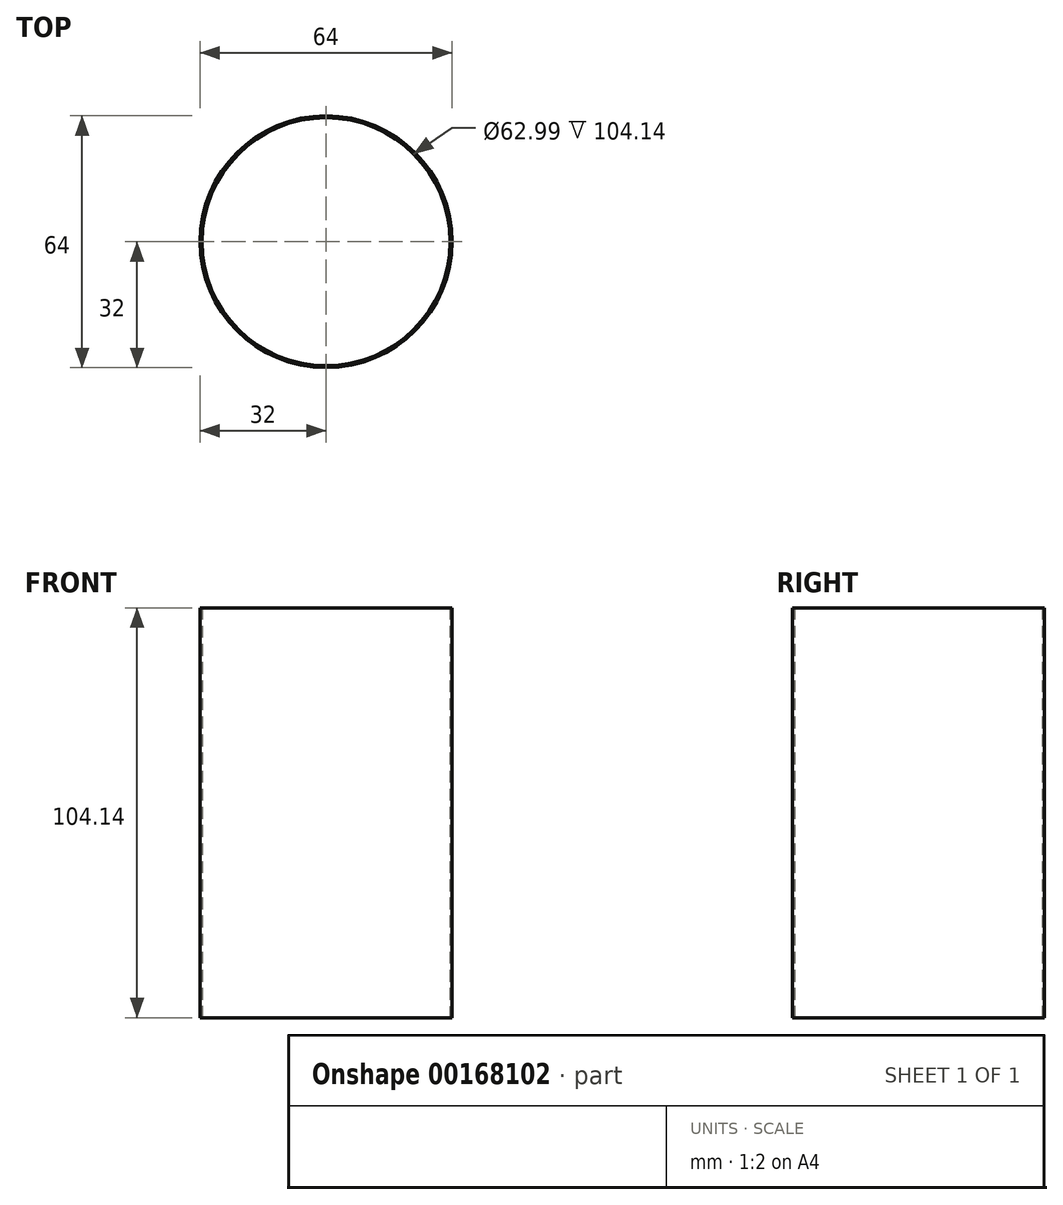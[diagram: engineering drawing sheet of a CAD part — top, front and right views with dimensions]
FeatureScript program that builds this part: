
annotation { "Feature Type Name" : "Feature", "Feature Type Description" : "" }
export const myFeature = defineFeature(function(context is Context, id is Id, definition is map)
    precondition{}
    {
        {
            var Q0;
            Q0=qCreatedBy(makeId("Top.planeOp"),FACE);
            var sketch = newSketch(context, id + "F0", { "sketchPlane" : qUnion([Q0])});
            skCircle(sketch, "E0", {"center": v(0, 0) * mm, "radius": 32 * mm});
            skCircle(sketch, "E1", {"center": v(0, 0) * mm, "radius": 31.5 * mm});
            skSolve(sketch);
        }
        {
            var Q0;
            Q0=qSketchRegion(id+"F0",true);
            extrude(context, id + "F1", {"entities" : qUnion([Q0]), "depth" : 104.14 * mm});
        }
    });
